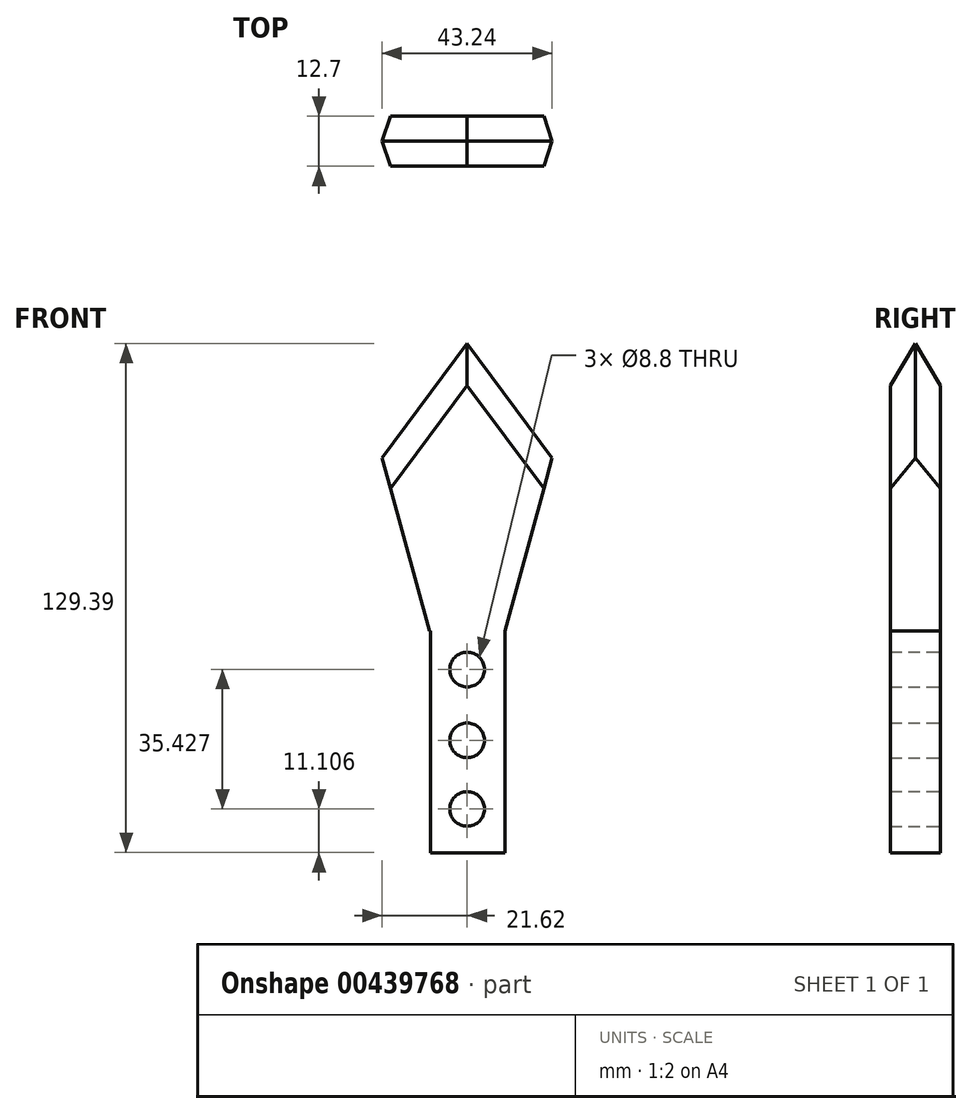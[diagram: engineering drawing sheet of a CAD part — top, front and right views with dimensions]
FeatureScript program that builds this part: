
annotation { "Feature Type Name" : "Feature", "Feature Type Description" : "" }
export const myFeature = defineFeature(function(context is Context, id is Id, definition is map)
    precondition{}
    {
        {
            var Q0;
            Q0=qCreatedBy(makeId("Front.planeOp"),FACE);
            var sketch = newSketch(context, id + "F0", { "sketchPlane" : qUnion([Q0])});
            skLineSegment(sketch, "E0.bottom", {"start": v(9.6, 0) * mm, "end": v(-9.3, 0) * mm});
            skLineSegment(sketch, "E0.top", {"start": v(9.6, -56.3) * mm, "end": v(-9.3, -56.3) * mm});
            skLineSegment(sketch, "E0.left", {"start": v(9.6, 0) * mm, "end": v(9.6, -56.3) * mm});
            skLineSegment(sketch, "E0.right", {"start": v(-9.3, 0) * mm, "end": v(-9.3, -56.3) * mm});
            skSolve(sketch);
        }
        {
            var Q0;
            Q0=makeQuery(id+"F0.imprint","IMPRINT",FACE,{"disambiguationData":[TD([[makeQuery(id+"F0.imprint","IMPRINT",EDGE,{"derivedFrom":sQuery(id+"F0.wireOp",EDGE,"E0.bottom")}),1.0]])]});
            extrude(context, id + "F1", {"entities" : qUnion([Q0]), "depth" : 12.7 * mm});
        }
        {
            var Q0;
            Q0=qCreatedBy(makeId("Front.planeOp"),FACE);
            var sketch = newSketch(context, id + "F2", { "sketchPlane" : qUnion([Q0])});
            skPoint(sketch, "E1", {"position": v(0, -9.76) * mm});
            skPoint(sketch, "E2", {"position": v(0, -27.77) * mm});
            skPoint(sketch, "E3", {"position": v(0, -45.18) * mm});
            skSolve(sketch);
        }
        {
            var Q0;
            Q0=sQuery(id+"F2.wireOp",VERTEX,"E1");
            var Q1;
            Q1=sQuery(id+"F2.wireOp",VERTEX,"E2");
            var Q2;
            Q2=sQuery(id+"F2.wireOp",VERTEX,"E3");
            var Q3;
            Q3=makeQuery(id+"F1.opExtrude","SWEPT_BODY",BODY,{"disambiguationData":[OSD([sQuery(id+"F0.wireOp",EDGE,"E0.bottom"),sQuery(id+"F0.wireOp",EDGE,"E0.top"),sQuery(id+"F0.wireOp",EDGE,"E0.left"),sQuery(id+"F0.wireOp",EDGE,"E0.right")])]});
            hole(context, id + "F3", {"style" : HoleStyle.SIMPLE, "endStyle" : HoleEndStyle.THROUGH, "oppositeDirection" : true, "standardTappedOrClearance" : lookupTablePath({ "standard" : "ISO", "fit" : "Normal", "size" : "M8", "type" : "Clearance" }), "standardBlindInLast" : lookupTablePath({ "fit" : "Standard", "standard" : "ISO", "size" : "M8", "type" : "Clearance" }), "holeDiameter" : 8.8 * mm, "isTappedThrough" : true, "tappedDepth" : 12.7 * mm, "tapClearance" : 3, "locations" : qUnion([Q0, Q1, Q2]), "scope" : qUnion([Q3])});
        }
        {
            var Q0;
            Q0=qCreatedBy(makeId("Front.planeOp"),FACE);
            var sketch = newSketch(context, id + "F4", { "sketchPlane" : qUnion([Q0])});
            skLineSegment(sketch, "E4", {"start": v(9.6, 0) * mm, "end": v(21.62, 43.98) * mm});
            skLineSegment(sketch, "E5", {"start": v(21.62, 43.98) * mm, "end": v(0, 73.1) * mm});
            skLineSegment(sketch, "E6.MirrorCS", {"start": v(-21.62, 43.98) * mm, "end": v(0, 73.1) * mm});
            skLineSegment(sketch, "E7.MirrorCS", {"start": v(-9.6, 0) * mm, "end": v(-21.62, 43.98) * mm});
            skLineSegment(sketch, "E8", {"start": v(9.6, 0) * mm, "end": v(-9.6, 0) * mm});
            skLineSegment(sketch, "E9", {"start": v(-9.6, 0) * mm, "end": v(0, 0) * mm});
            skLineSegment(sketch, "E10", {"start": v(0, 0) * mm, "end": v(9.6, 0) * mm});
            skSolve(sketch);
        }
        {
            var Q0;
            Q0=makeQuery(id+"F4.imprint","IMPRINT",FACE,{"disambiguationData":[TD([[makeQuery(id+"F4.imprint","IMPRINT",EDGE,{"derivedFrom":sQuery(id+"F4.wireOp",EDGE,"E4")}),1.0]])]});
            extrude(context, id + "F5", {"entities" : qUnion([Q0]), "operationType" : NewBodyOperationType.ADD, "depth" : 12.7 * mm});
        }
        {
            var Q0;
            Q0=makeQuery(id+"F5.opExtrude","CAP_EDGE",EDGE,{"disambiguationData":[OSD([sQuery(id+"F4.wireOp",EDGE,"E5")])],"isStart":true});
            var Q1;
            Q1=makeQuery(id+"F5.opExtrude","CAP_EDGE",EDGE,{"disambiguationData":[OSD([sQuery(id+"F4.wireOp",EDGE,"E6.MirrorCS")])],"isStart":true});
            var Q2;
            Q2=makeQuery(id+"F5.opExtrude","CAP_EDGE",EDGE,{"disambiguationData":[OSD([sQuery(id+"F4.wireOp",EDGE,"E5")])],"isStart":false});
            var Q3;
            Q3=makeQuery(id+"F5.opExtrude","CAP_EDGE",EDGE,{"disambiguationData":[OSD([sQuery(id+"F4.wireOp",EDGE,"E6.MirrorCS")])],"isStart":false});
            chamfer(context, id + "F6", {"entities" : qUnion([Q0, Q1, Q2, Q3]), "width" : 6.35 * mm, "tangentPropagation" : true});
        }
    });
